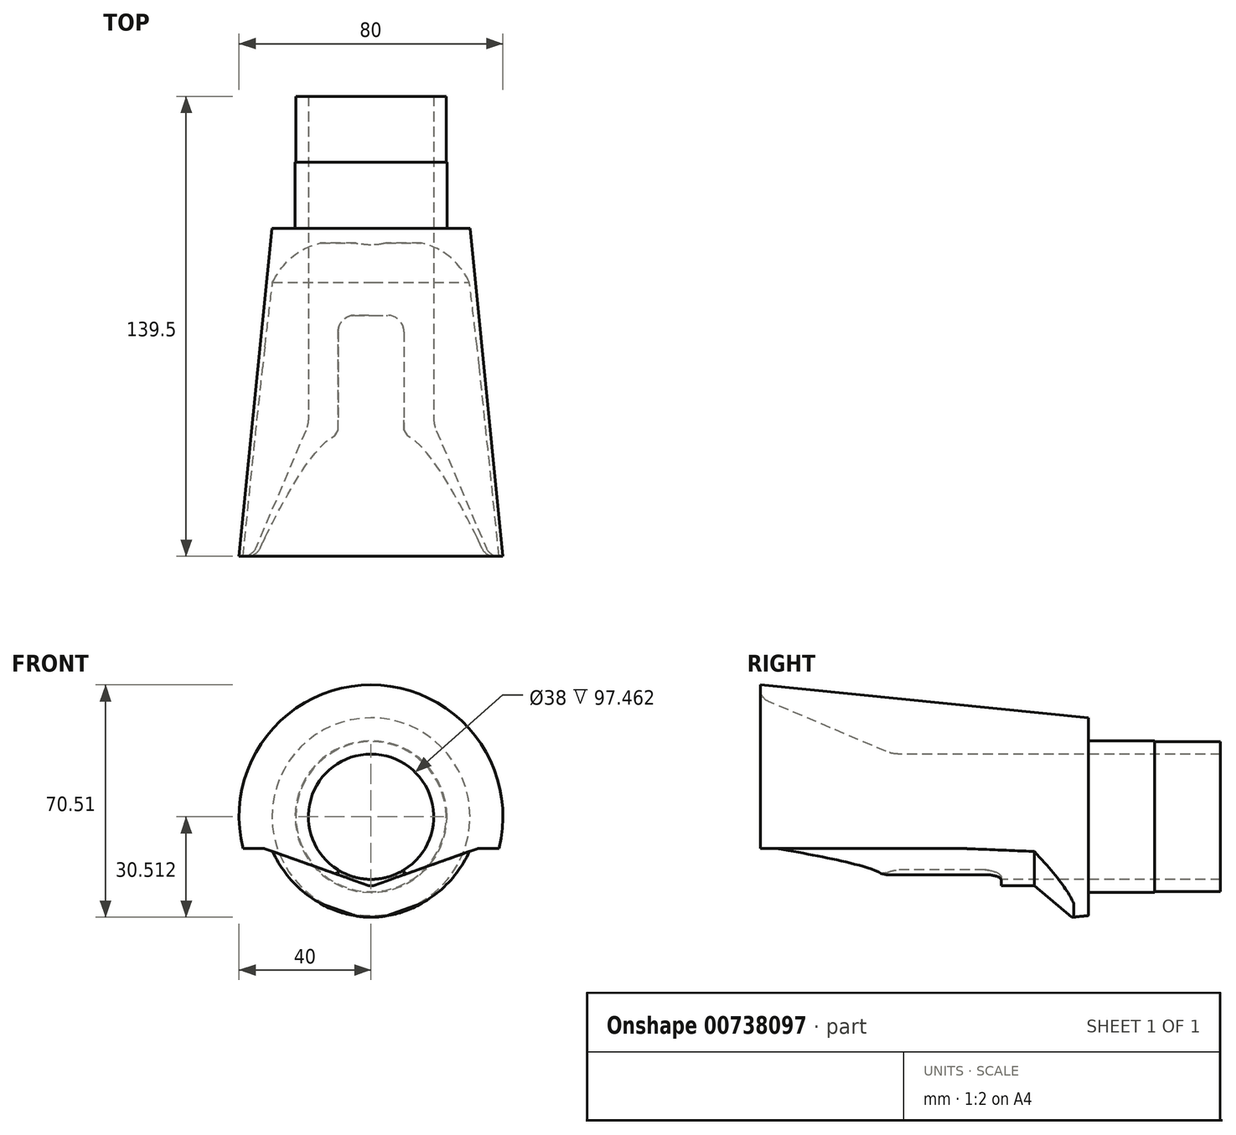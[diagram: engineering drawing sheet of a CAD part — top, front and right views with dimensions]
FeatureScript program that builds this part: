
annotation { "Feature Type Name" : "Feature", "Feature Type Description" : "" }
export const myFeature = defineFeature(function(context is Context, id is Id, definition is map)
    precondition{}
    {
        {
            var Q0;
            Q0=qCreatedBy(makeId("Right.planeOp"),FACE);
            var sketch = newSketch(context, id + "F0", { "sketchPlane" : qUnion([Q0])});
            skLineSegment(sketch, "E0", {"start": v(0, 94.62) * mm, "end": v(-99.5, 104.62) * mm});
            skLineSegment(sketch, "E1", {"start": v(-99.5, 104.62) * mm, "end": v(-99.5, 103.27) * mm});
            skLineSegment(sketch, "E2", {"start": v(-57.46, 83.62) * mm, "end": v(40, 83.62) * mm});
            skLineSegment(sketch, "E3", {"start": v(40, 83.62) * mm, "end": v(40, 87.37) * mm});
            skLineSegment(sketch, "E4", {"start": v(40, 87.37) * mm, "end": v(20, 87.37) * mm});
            skLineSegment(sketch, "E5", {"start": v(20, 87.37) * mm, "end": v(20, 87.62) * mm});
            skLineSegment(sketch, "E6", {"start": v(20, 87.62) * mm, "end": v(0, 87.62) * mm});
            skLineSegment(sketch, "E7", {"start": v(0, 87.62) * mm, "end": v(0, 94.62) * mm});
            skLineSegment(sketch, "E8", {"start": v(-115.5, 64.62) * mm, "end": v(75.13, 64.62) * mm, "construction": true});
            skLineSegment(sketch, "E9", {"start": v(-61.37, 84.42) * mm, "end": v(-97.06, 99.59) * mm});
            skPoint(sketch, "E10.orphan", {"position": v(-99.5, 83.62) * mm});
            skPoint(sketch, "E11.visualSharp", {"position": v(-99.5, 100.62) * mm});
            skArc(sketch, "E11.filletArc", {"start": v(-99.5, 103.27) * mm, "mid": v(-98.83, 101.06) * mm, "end": v(-97.06, 99.59) * mm});
            skPoint(sketch, "E12.visualSharp", {"position": v(-59.5, 83.62) * mm});
            skArc(sketch, "E12.filletArc", {"start": v(-61.37, 84.42) * mm, "mid": v(-59.46, 83.82) * mm, "end": v(-57.46, 83.62) * mm});
            skSolve(sketch);
        }
        {
            var Q0;
            Q0=makeQuery(id+"F0.imprint","IMPRINT",FACE,{"disambiguationData":[TD([[makeQuery(id+"F0.imprint","IMPRINT",EDGE,{"derivedFrom":sQuery(id+"F0.wireOp",EDGE,"E0")}),1.0]])]});
            var Q1;
            Q1=sQuery(id+"F0.wireOp",EDGE,"E8");
            revolve(context, id + "F1", {"surfaceOperationType" : NewSurfaceOperationType.NEW, "entities" : qUnion([Q0]), "axis" : qUnion([Q1]), "revolveType" : RevolveType.FULL});
        }
        {
            var Q0;
            Q0=makeQuery(id+"F1.opRevolve","SWEPT_FACE",FACE,{"disambiguationData":[OSD([sQuery(id+"F0.wireOp",EDGE,"E1")])]});
            var sketch = newSketch(context, id + "F2", { "sketchPlane" : qUnion([Q0])});
            skLineSegment(sketch, "E13", {"start": v(0, 19) * mm, "end": v(41, 19) * mm});
            skLineSegment(sketch, "E14", {"start": v(41, 19) * mm, "end": v(41, 55) * mm});
            skLineSegment(sketch, "E15", {"start": v(41, 55) * mm, "end": v(32.84, 55) * mm});
            skLineSegment(sketch, "E16", {"start": v(32.18, 54.89) * mm, "end": v(0.67, 43.74) * mm});
            skLineSegment(sketch, "E17.MirrorCS", {"start": v(-32.18, 54.89) * mm, "end": v(-0.67, 43.74) * mm});
            skLineSegment(sketch, "E18.MirrorCS", {"start": v(-41, 55) * mm, "end": v(-32.84, 55) * mm});
            skLineSegment(sketch, "E19.MirrorCS", {"start": v(-41, 19) * mm, "end": v(-41, 55) * mm});
            skLineSegment(sketch, "E20.MirrorCS", {"start": v(0, 19) * mm, "end": v(-41, 19) * mm});
            skPoint(sketch, "E21.visualSharp", {"position": v(-32.5, 55) * mm});
            skArc(sketch, "E21.filletArc", {"start": v(-32.18, 54.89) * mm, "mid": v(-32.5, 54.97) * mm, "end": v(-32.84, 55) * mm});
            skPoint(sketch, "E22.visualSharp", {"position": v(0, 43.5) * mm});
            skArc(sketch, "E22.filletArc", {"start": v(-0.67, 43.74) * mm, "mid": v(0, 43.62) * mm, "end": v(0.67, 43.74) * mm});
            skPoint(sketch, "E23.visualSharp", {"position": v(32.5, 55) * mm});
            skArc(sketch, "E23.filletArc", {"start": v(32.84, 55) * mm, "mid": v(32.5, 54.97) * mm, "end": v(32.18, 54.89) * mm});
            skSolve(sketch);
        }
        {
            var Q0;
            {var subQ0=sQuery(id+"F2.wireOp",EDGE,"E15");var subQ1=sQuery(id+"F0.wireOp",EDGE,"E1");var subQ2=makeQuery(id+"F1.opRevolve","SWEPT_EDGE",EDGE,{"disambiguationData":[OSD([sQuery(id+"F0.wireOp",EDGE,"E0"),subQ1])]});var subQ3=makeQuery(id+"F2.imprint","INTERSECT",VERTEX,{"derivedFrom":[subQ2,subQ0]});Q0=makeQuery(id+"F2.imprint","IMPRINT",FACE,{"disambiguationData":[TD([[makeQuery(id+"F2.imprint","IMPRINT",EDGE,{"disambiguationData":[TD([[subQ3,-1.0]])],"derivedFrom":subQ0}),1.0]])]});}
            var Q1;
            Q1=makeQuery(id+"F2.imprint","IMPRINT",FACE,{"disambiguationData":[TD([[makeQuery(id+"F2.imprint","IMPRINT",EDGE,{"derivedFrom":sQuery(id+"F2.wireOp",EDGE,"E16")}),1.0]])]});
            extrude(context, id + "F3", {"entities" : qUnion([Q0, Q1]), "operationType" : NewBodyOperationType.REMOVE, "oppositeDirection" : true, "depth" : 95 * mm, "offsetDistance" : 25 * mm});
        }
        {
            var Q0;
            Q0=makeQuery(id+"F3.boolean.opBoolean","COPY",EDGE,{"derivedFrom":makeQuery(id+"F3.opExtrude","CAP_EDGE",EDGE,{"disambiguationData":[OSD([sQuery(id+"F2.wireOp",EDGE,"E16")])],"isStart":false})});
            chamfer(context, id + "F4", {"entities" : qUnion([Q0]), "chamferType" : ChamferType.OFFSET_ANGLE, "width" : 10 * mm, "oppositeDirection" : false, "angle" : 50 * degree, "tangentPropagation" : true});
        }
        {
            var Q0;
            Q0=qCreatedBy(makeId("Top.planeOp"),FACE);
            cPlane(context, id + "F5", {"entities" : qUnion([Q0]), "cplaneType" : CPlaneType.OFFSET, "offset" : 43 * mm, "width" : 150 * mm, "height" : 150 * mm});
        }
        {
            var Q0;
            Q0=qCreatedBy(id+"F5.planeOp",FACE);
            var sketch = newSketch(context, id + "F6", { "sketchPlane" : qUnion([Q0])});
            skLineSegment(sketch, "E24.bottom", {"start": v(10, -66.42) * mm, "end": v(-10, -66.42) * mm});
            skLineSegment(sketch, "E24.top", {"start": v(5, -26.42) * mm, "end": v(-5, -26.42) * mm});
            skLineSegment(sketch, "E24.left", {"start": v(10, -61.22) * mm, "end": v(10, -31.42) * mm});
            skLineSegment(sketch, "E24.right", {"start": v(-10, -61.22) * mm, "end": v(-10, -31.42) * mm});
            skPoint(sketch, "E24.middle", {"position": v(0, -46.42) * mm});
            skPoint(sketch, "E25.visualSharp", {"position": v(-10, -26.42) * mm});
            skArc(sketch, "E25.filletArc", {"start": v(-5, -26.42) * mm, "mid": v(-8.54, -27.88) * mm, "end": v(-10, -31.42) * mm});
            skPoint(sketch, "E26.visualSharp", {"position": v(10, -26.42) * mm});
            skArc(sketch, "E26.filletArc", {"start": v(10, -31.42) * mm, "mid": v(8.54, -27.88) * mm, "end": v(5, -26.42) * mm});
            skLineSegment(sketch, "E27", {"start": v(-10, -66.42) * mm, "end": v(-13, -66.42) * mm});
            skLineSegment(sketch, "E28", {"start": v(10, -66.42) * mm, "end": v(13, -66.42) * mm});
            skLineSegment(sketch, "E29", {"start": v(-13, -66.42) * mm, "end": v(-10, -61.22) * mm});
            skLineSegment(sketch, "E30", {"start": v(13, -66.42) * mm, "end": v(10, -61.22) * mm});
            skSolve(sketch);
        }
        {
            var Q0;
            Q0=makeQuery(id+"F6.imprint","IMPRINT",FACE,{"disambiguationData":[TD([[makeQuery(id+"F6.imprint","IMPRINT",EDGE,{"derivedFrom":sQuery(id+"F6.wireOp",EDGE,"E24.bottom")}),-1.0]])]});
            extrude(context, id + "F7", {"entities" : qUnion([Q0]), "operationType" : NewBodyOperationType.REMOVE, "depth" : 10 * mm, "offsetDistance" : 25 * mm});
        }
    });
